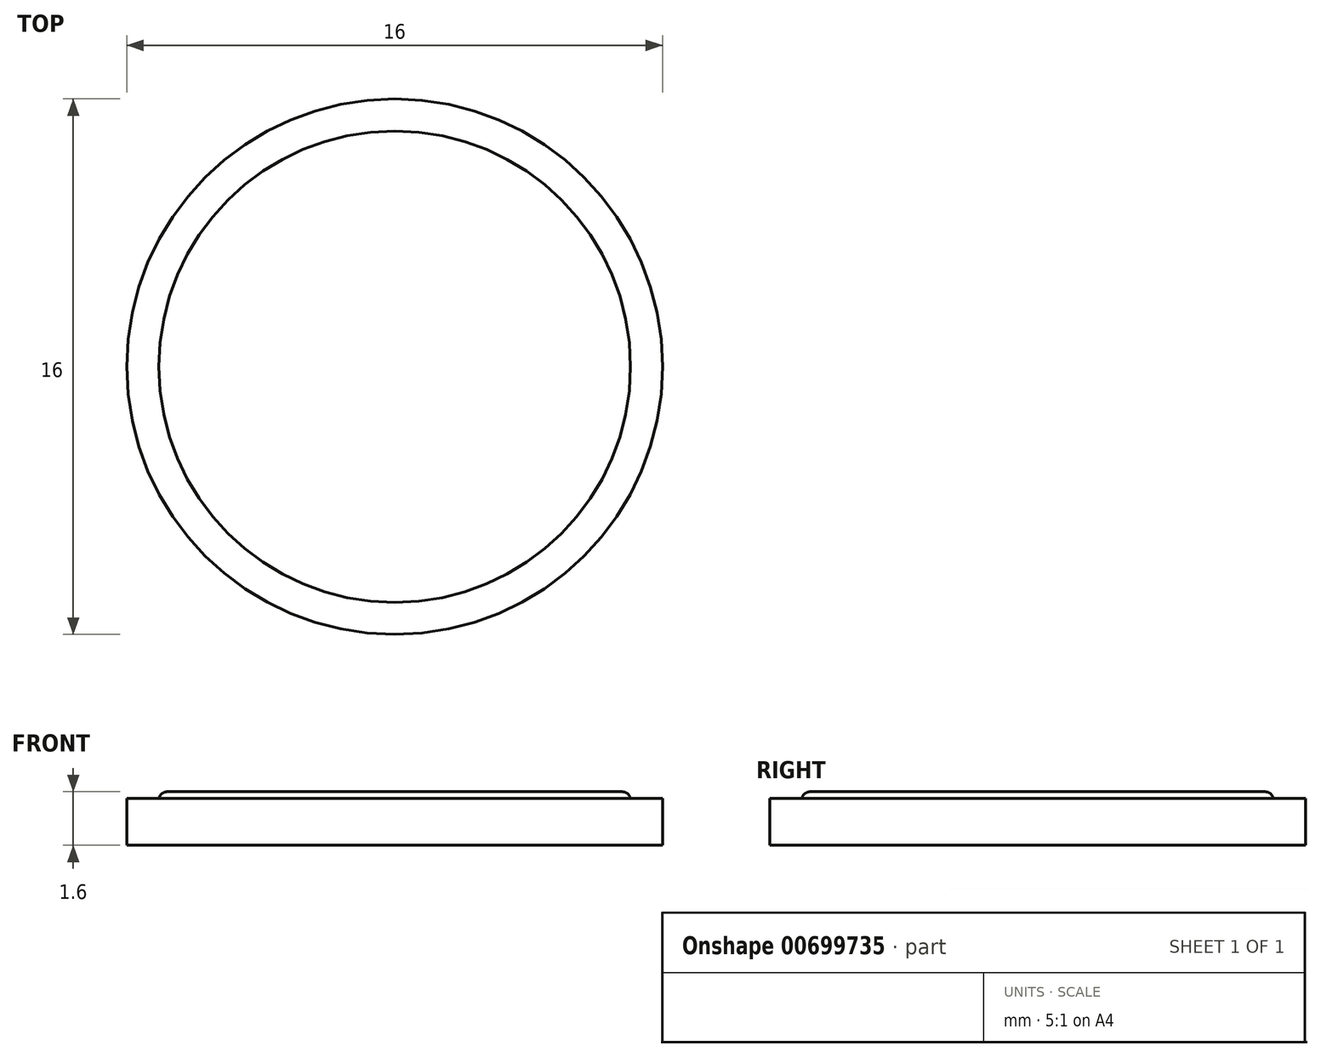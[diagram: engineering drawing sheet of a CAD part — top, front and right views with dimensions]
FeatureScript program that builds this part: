
annotation { "Feature Type Name" : "Feature", "Feature Type Description" : "" }
export const myFeature = defineFeature(function(context is Context, id is Id, definition is map)
    precondition{}
    {
        {
            var Q0;
            Q0=qCreatedBy(makeId("Front.planeOp"),FACE);
            var sketch = newSketch(context, id + "F0", { "sketchPlane" : qUnion([Q0])});
            skLineSegment(sketch, "E0", {"start": v(0, 0) * mm, "end": v(8, 0) * mm});
            skLineSegment(sketch, "E1", {"start": v(8, 0) * mm, "end": v(8, 1.4) * mm});
            skLineSegment(sketch, "E2", {"start": v(8, 1.4) * mm, "end": v(7.04, 1.4) * mm});
            skLineSegment(sketch, "E3", {"start": v(0, 1.6) * mm, "end": v(0, 0) * mm});
            skPoint(sketch, "E4.visualSharp", {"position": v(7, 1.6) * mm});
            skLineSegment(sketch, "E5", {"start": v(7.04, 1.4) * mm, "end": v(7.04, 1.4) * mm});
            skLineSegment(sketch, "E6", {"start": v(0, 1.6) * mm, "end": v(6.8, 1.6) * mm});
            skArc(sketch, "E7.filletArc", {"start": v(7.04, 1.4) * mm, "mid": v(6.95, 1.54) * mm, "end": v(6.8, 1.6) * mm});
            skSolve(sketch);
        }
        {
            var Q0;
            Q0=makeQuery(id+"F0.imprint","IMPRINT",FACE,{"disambiguationData":[TD([[makeQuery(id+"F0.imprint","IMPRINT",EDGE,{"derivedFrom":sQuery(id+"F0.wireOp",EDGE,"E0")}),1.0]])]});
            var Q1;
            Q1=sQuery(id+"F0.wireOp",EDGE,"E3");
            revolve(context, id + "F1", {"entities" : qUnion([Q0]), "axis" : qUnion([Q1]), "revolveType" : RevolveType.FULL});
        }
    });
